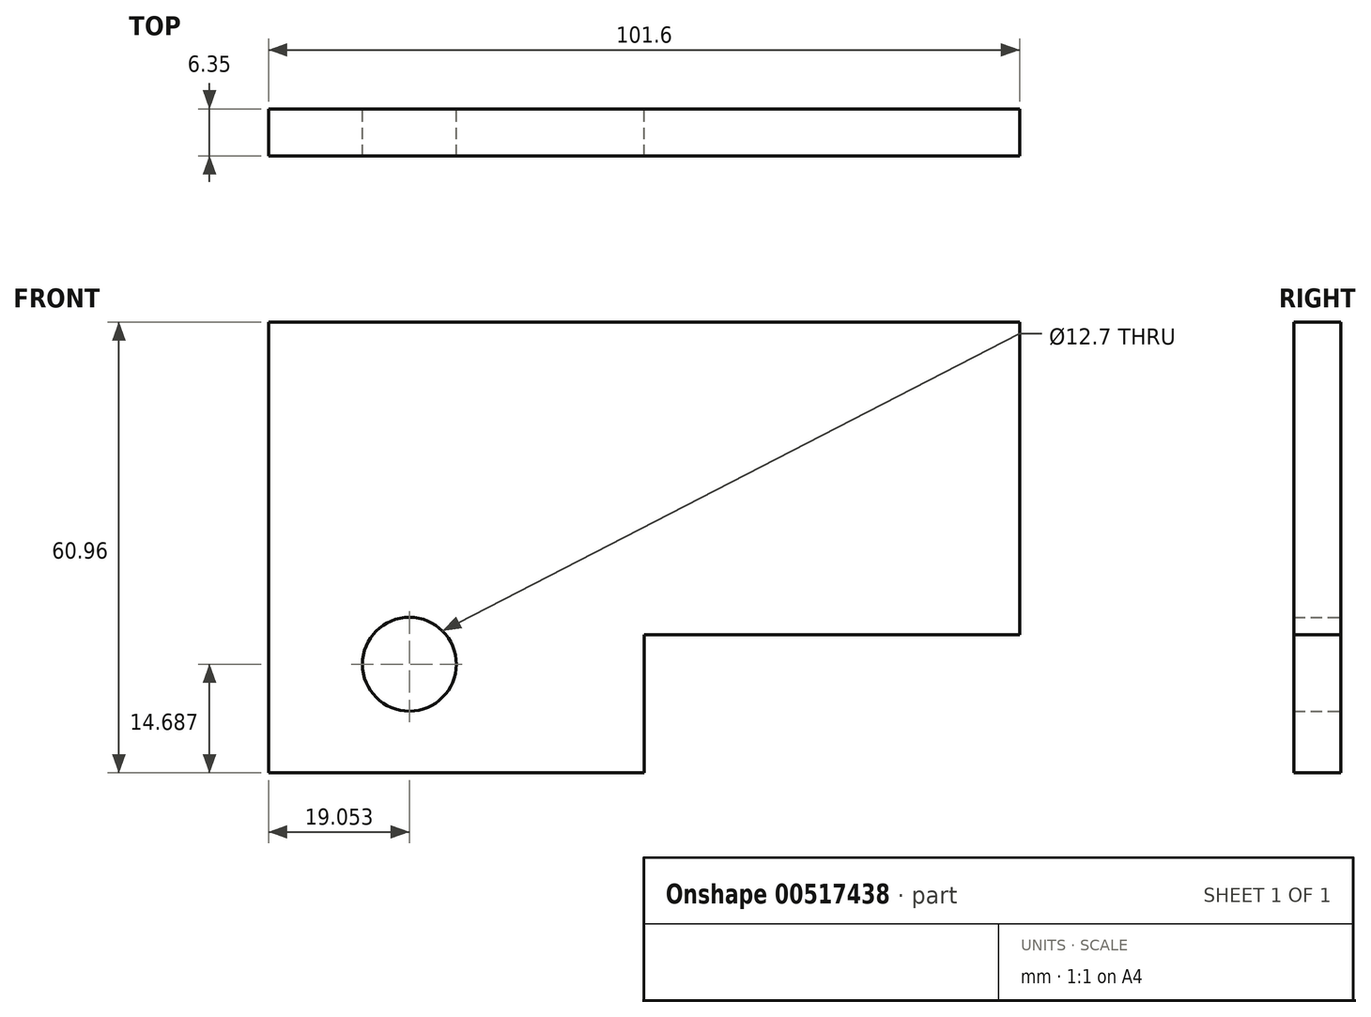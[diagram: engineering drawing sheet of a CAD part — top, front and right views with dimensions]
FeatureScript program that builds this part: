
annotation { "Feature Type Name" : "Feature", "Feature Type Description" : "" }
export const myFeature = defineFeature(function(context is Context, id is Id, definition is map)
    precondition{}
    {
        {
            var Q0;
            Q0=qCreatedBy(makeId("Front.planeOp"),FACE);
            var sketch = newSketch(context, id + "F0", { "sketchPlane" : qUnion([Q0])});
            skLineSegment(sketch, "E0", {"start": v(-49.3, 28.58) * mm, "end": v(52.3, 28.58) * mm});
            skLineSegment(sketch, "E1", {"start": v(52.3, 28.58) * mm, "end": v(52.3, -13.69) * mm});
            skLineSegment(sketch, "E2", {"start": v(52.3, -13.69) * mm, "end": v(1.5, -13.69) * mm});
            skLineSegment(sketch, "E3", {"start": v(1.5, -13.69) * mm, "end": v(1.5, -32.38) * mm});
            skLineSegment(sketch, "E4", {"start": v(1.5, -32.38) * mm, "end": v(-49.3, -32.38) * mm});
            skLineSegment(sketch, "E5", {"start": v(-49.3, -32.38) * mm, "end": v(-49.3, 28.58) * mm});
            skCircle(sketch, "E6", {"center": v(-30.25, -17.7) * mm, "radius": 6.35 * mm});
            skSolve(sketch);
        }
        {
            var Q0;
            Q0=makeQuery(id+"F0.imprint","IMPRINT",FACE,{"disambiguationData":[TD([[makeQuery(id+"F0.imprint","IMPRINT",EDGE,{"derivedFrom":sQuery(id+"F0.wireOp",EDGE,"E0")}),-1.0]])]});
            extrude(context, id + "F1", {"entities" : qUnion([Q0]), "depth" : 6.35 * mm, "offsetDistance" : 25.4 * mm});
        }
    });
